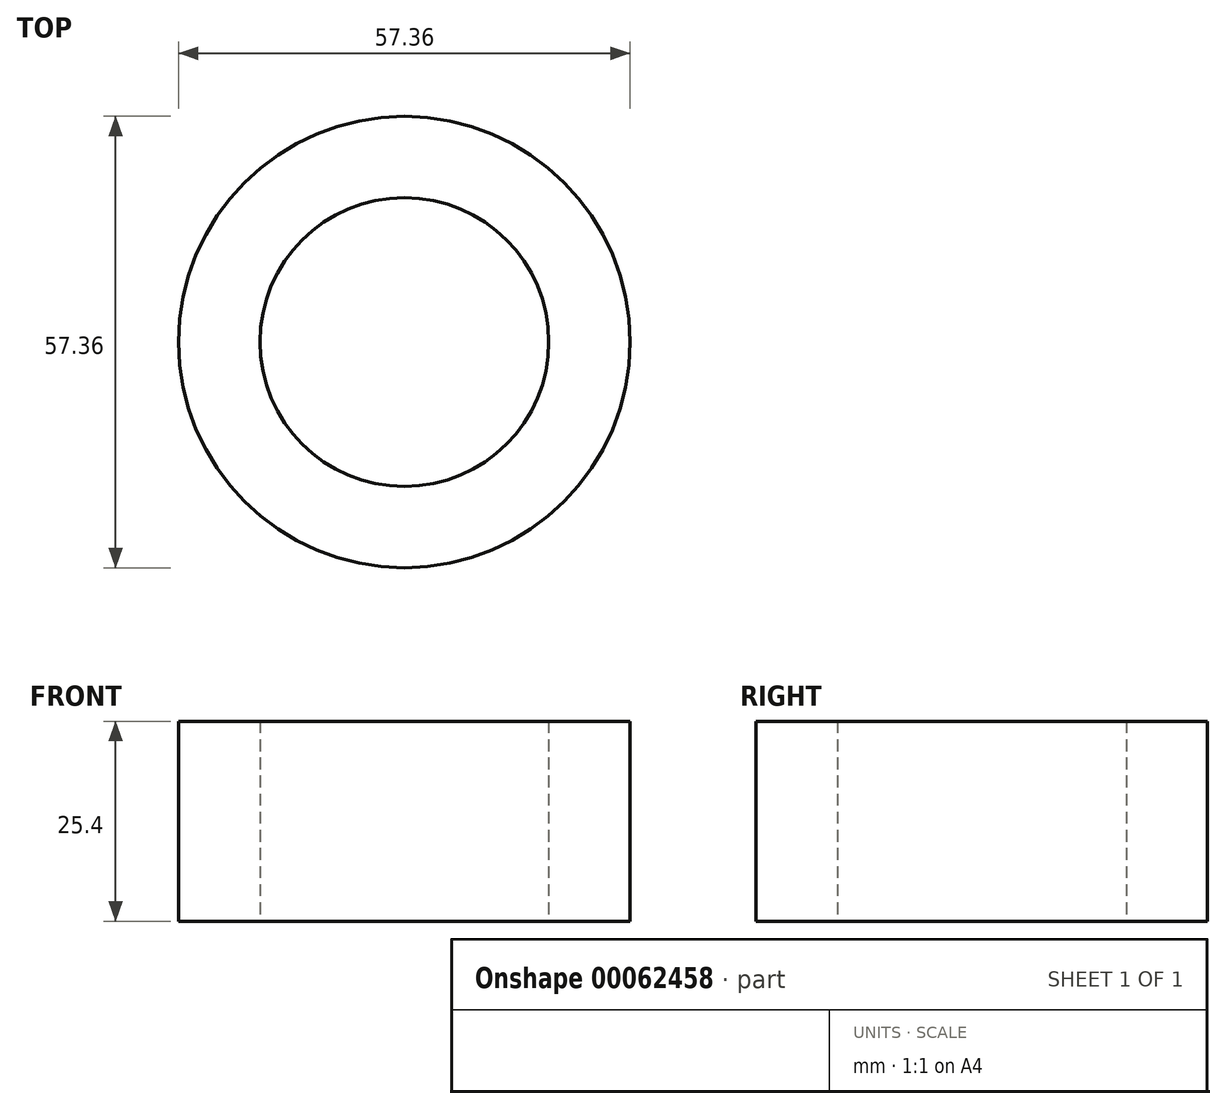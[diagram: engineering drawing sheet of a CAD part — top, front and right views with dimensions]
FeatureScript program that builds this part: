
annotation { "Feature Type Name" : "Feature", "Feature Type Description" : "" }
export const myFeature = defineFeature(function(context is Context, id is Id, definition is map)
    precondition{}
    {
        {
            var Q0;
            Q0=qCreatedBy(makeId("Top.planeOp"),FACE);
            var sketch = newSketch(context, id + "F0", { "sketchPlane" : qUnion([Q0])});
            skCircle(sketch, "E0", {"center": v(0, 0) * mm, "radius": 28.68 * mm});
            skSolve(sketch);
        }
        {
            var Q0;
            Q0=qCreatedBy(makeId("Top.planeOp"),FACE);
            var sketch = newSketch(context, id + "F1", { "sketchPlane" : qUnion([Q0])});
            skCircle(sketch, "E1", {"center": v(0, 0) * mm, "radius": 18.35 * mm});
            skSolve(sketch);
        }
        {
            var Q0;
            Q0=makeQuery(id+"F1.imprint","IMPRINT",FACE,{"disambiguationData":[TD([[makeQuery(id+"F1.imprint","IMPRINT",EDGE,{"derivedFrom":sQuery(id+"F1.wireOp",EDGE,"E1")}),1.0]])]});
            var Q1;
            Q1=makeQuery(id+"F0.imprint","IMPRINT",FACE,{"disambiguationData":[TD([[makeQuery(id+"F0.imprint","IMPRINT",EDGE,{"derivedFrom":sQuery(id+"F0.wireOp",EDGE,"E0")}),1.0]])]});
            extrude(context, id + "F2", {"entities" : qUnion([Q0, Q1]), "depth" : 25.4 * mm});
        }
    });
